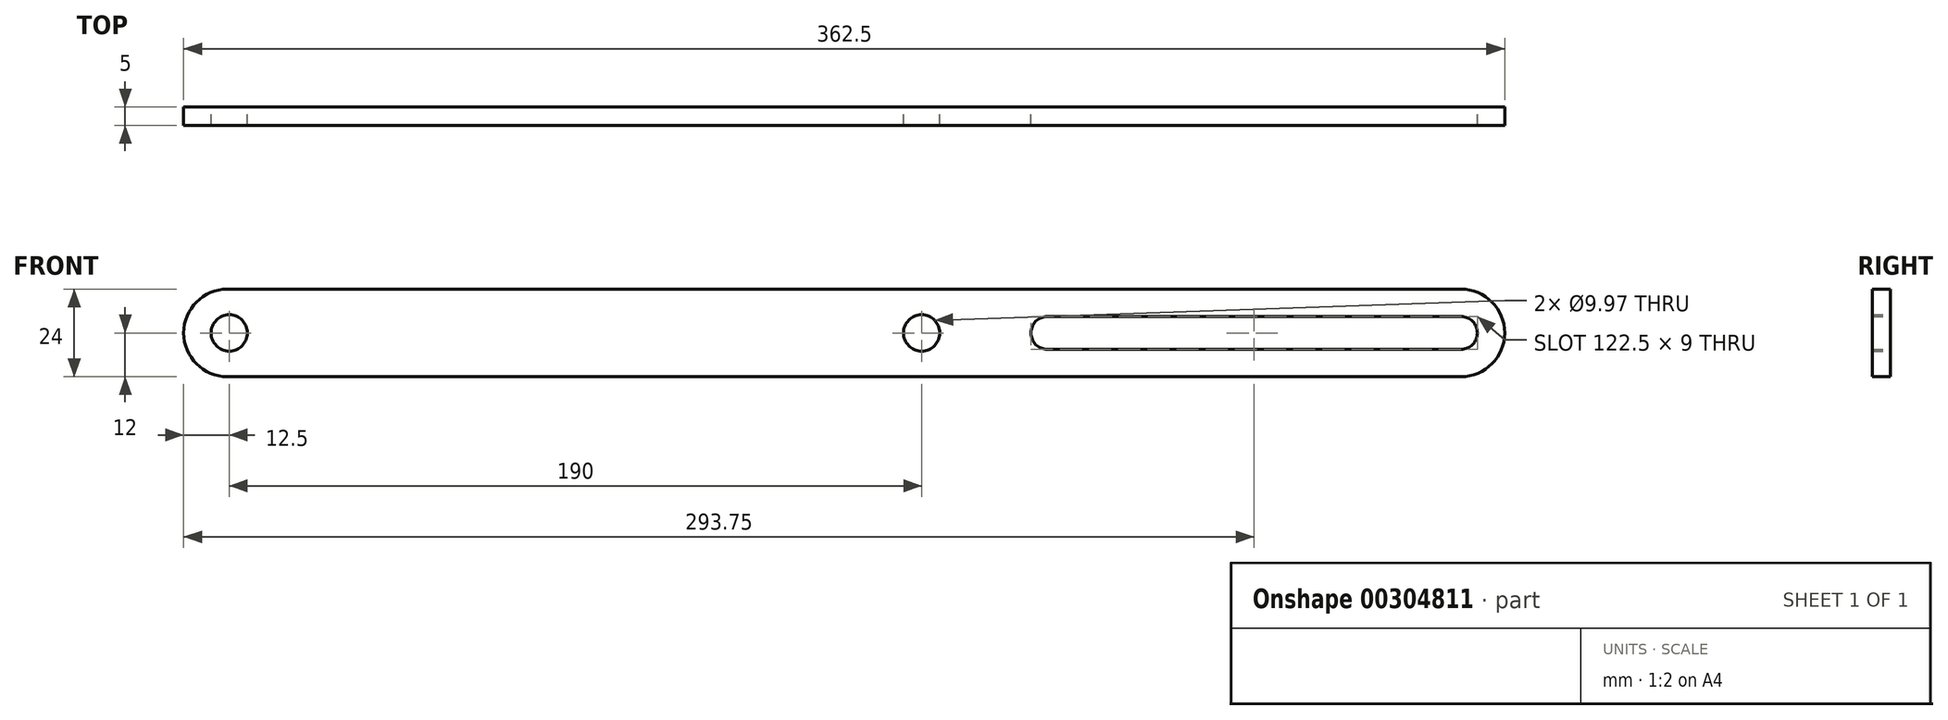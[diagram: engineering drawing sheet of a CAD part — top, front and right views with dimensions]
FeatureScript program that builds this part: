
annotation { "Feature Type Name" : "Feature", "Feature Type Description" : "" }
export const myFeature = defineFeature(function(context is Context, id is Id, definition is map)
    precondition{}
    {
        {
            var Q0;
            Q0=qCreatedBy(makeId("Front.planeOp"),FACE);
            var sketch = newSketch(context, id + "F0", { "sketchPlane" : qUnion([Q0])});
            skLineSegment(sketch, "E0.bottom", {"start": v(118, -12) * mm, "end": v(-220.5, -12) * mm});
            skLineSegment(sketch, "E0.top", {"start": v(118, 12) * mm, "end": v(-220.5, 12) * mm});
            skLineSegment(sketch, "E0.left", {"start": v(130, 0) * mm, "end": v(130, 0) * mm});
            skLineSegment(sketch, "E0.right", {"start": v(-232.5, 0) * mm, "end": v(-232.5, 0) * mm});
            skPoint(sketch, "E0.middle", {"position": v(0, 0) * mm});
            skCircle(sketch, "E1", {"center": v(-220, 0) * mm, "radius": 4.99 * mm});
            skLineSegment(sketch, "E2.bottom", {"start": v(118, -4.5) * mm, "end": v(4.5, -4.5) * mm});
            skLineSegment(sketch, "E2.top", {"start": v(118, 4.5) * mm, "end": v(4.5, 4.5) * mm});
            skLineSegment(sketch, "E2.left", {"start": v(122.5, 0) * mm, "end": v(122.5, 0) * mm});
            skLineSegment(sketch, "E2.right", {"start": v(0, 0) * mm, "end": v(0, 0) * mm});
            skPoint(sketch, "E2.middle", {"position": v(61.25, 0) * mm});
            skCircle(sketch, "E3", {"center": v(-30, 0) * mm, "radius": 4.99 * mm});
            skPoint(sketch, "E4.visualSharp", {"position": v(-232.5, 12) * mm});
            skArc(sketch, "E4.filletArc", {"start": v(-220.5, 12) * mm, "mid": v(-228.99, 8.49) * mm, "end": v(-232.5, 0) * mm});
            skPoint(sketch, "E5.visualSharp", {"position": v(-232.5, -12) * mm});
            skArc(sketch, "E5.filletArc", {"start": v(-232.5, 0) * mm, "mid": v(-228.99, -8.49) * mm, "end": v(-220.5, -12) * mm});
            skPoint(sketch, "E6.visualSharp", {"position": v(130, 12) * mm});
            skArc(sketch, "E6.filletArc", {"start": v(130, 0) * mm, "mid": v(126.49, 8.49) * mm, "end": v(118, 12) * mm});
            skPoint(sketch, "E7.visualSharp", {"position": v(130, -12) * mm});
            skArc(sketch, "E7.filletArc", {"start": v(118, -12) * mm, "mid": v(126.49, -8.49) * mm, "end": v(130, 0) * mm});
            skPoint(sketch, "E8.visualSharp", {"position": v(122.5, 4.5) * mm});
            skPoint(sketch, "E9.visualSharp", {"position": v(122.5, -4.5) * mm});
            skPoint(sketch, "E10.visualSharp", {"position": v(0, 4.5) * mm});
            skPoint(sketch, "E11.visualSharp", {"position": v(0, -4.5) * mm});
            skArc(sketch, "E12.filletArc", {"start": v(4.5, 4.5) * mm, "mid": v(1.32, 3.18) * mm, "end": v(0, 0) * mm});
            skArc(sketch, "E13.filletArc", {"start": v(0, 0) * mm, "mid": v(1.32, -3.18) * mm, "end": v(4.5, -4.5) * mm});
            skArc(sketch, "E14.filletArc", {"start": v(122.5, 0) * mm, "mid": v(121.18, 3.18) * mm, "end": v(118, 4.5) * mm});
            skArc(sketch, "E15.filletArc", {"start": v(118, -4.5) * mm, "mid": v(121.18, -3.18) * mm, "end": v(122.5, 0) * mm});
            skSolve(sketch);
        }
        {
            var Q0;
            Q0=makeQuery(id+"F0.imprint","IMPRINT",FACE,{"disambiguationData":[TD([[makeQuery(id+"F0.imprint","IMPRINT",EDGE,{"derivedFrom":sQuery(id+"F0.wireOp",EDGE,"E0.bottom")}),-1.0]])]});
            extrude(context, id + "F1", {"entities" : qUnion([Q0]), "depth" : 5 * mm});
        }
    });
